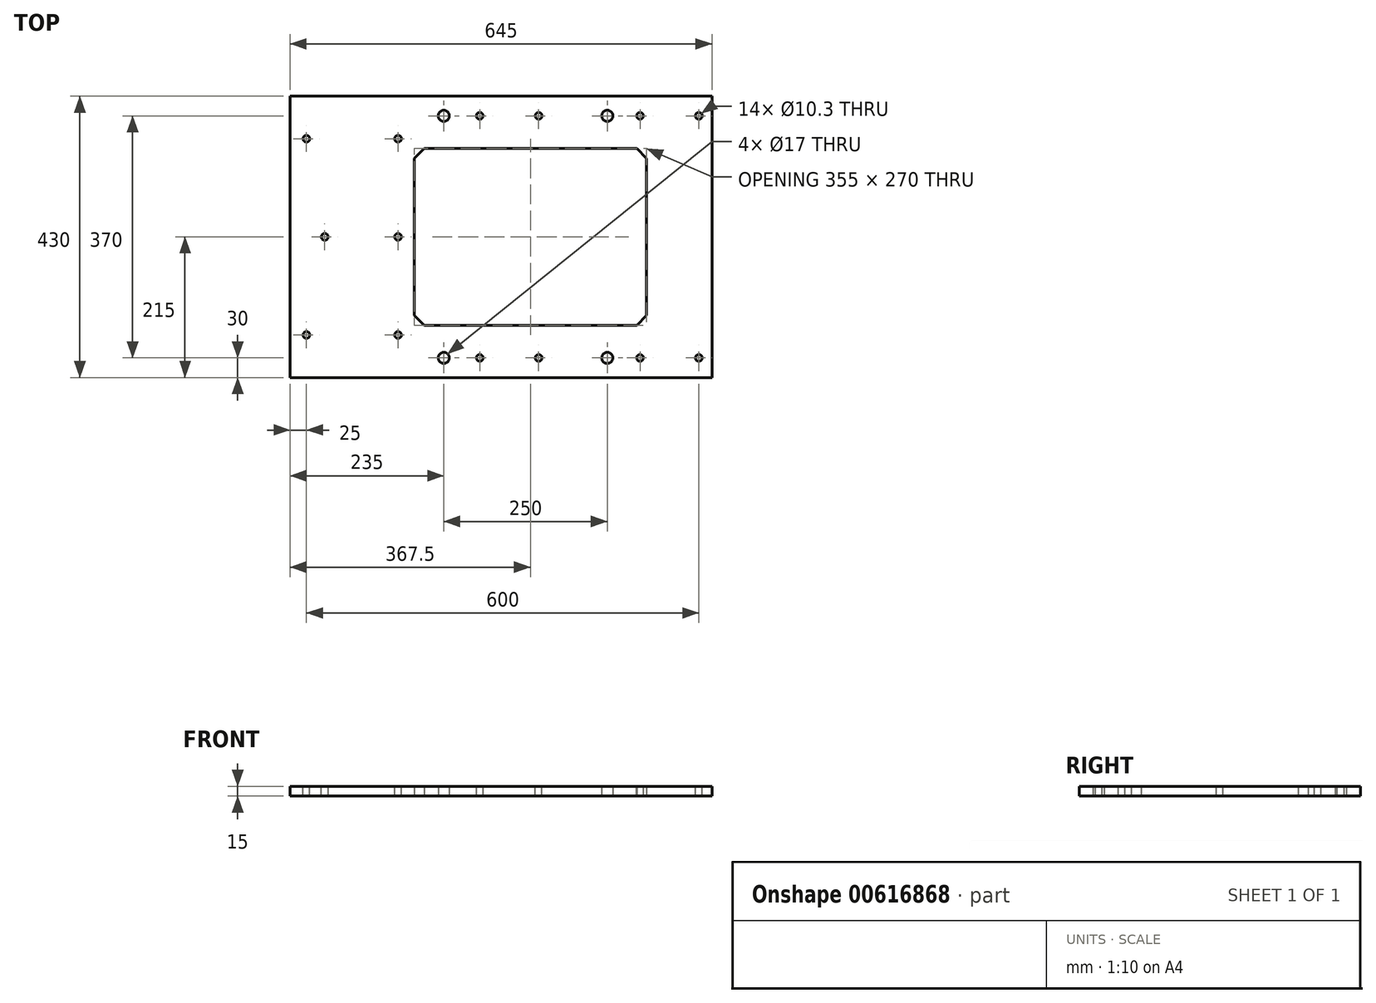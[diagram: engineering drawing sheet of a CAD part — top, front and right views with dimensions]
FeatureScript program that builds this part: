
annotation { "Feature Type Name" : "Feature", "Feature Type Description" : "" }
export const myFeature = defineFeature(function(context is Context, id is Id, definition is map)
    precondition{}
    {
        {
            var Q0;
            Q0=qCreatedBy(makeId("Top.planeOp"),FACE);
            var sketch = newSketch(context, id + "F0", { "sketchPlane" : qUnion([Q0])});
            skLineSegment(sketch, "E0.bottom", {"start": v(322.5, 215) * mm, "end": v(-322.5, 215) * mm});
            skLineSegment(sketch, "E0.top", {"start": v(322.5, -215) * mm, "end": v(-322.5, -215) * mm});
            skLineSegment(sketch, "E0.left", {"start": v(322.5, 215) * mm, "end": v(322.5, -215) * mm});
            skLineSegment(sketch, "E0.right", {"start": v(-322.5, 215) * mm, "end": v(-322.5, -215) * mm});
            skPoint(sketch, "E0.middle", {"position": v(0, 0) * mm});
            skLineSegment(sketch, "E1.bottom", {"start": v(-117.5, 135) * mm, "end": v(207.5, 135) * mm});
            skLineSegment(sketch, "E1.top", {"start": v(-117.5, -135) * mm, "end": v(207.5, -135) * mm});
            skLineSegment(sketch, "E1.left", {"start": v(-132.5, 120) * mm, "end": v(-132.5, -120) * mm});
            skLineSegment(sketch, "E1.right", {"start": v(222.5, 120) * mm, "end": v(222.5, -120) * mm});
            skLineSegment(sketch, "E2", {"start": v(-132.5, 120) * mm, "end": v(-117.5, 135) * mm});
            skLineSegment(sketch, "E3", {"start": v(207.5, 135) * mm, "end": v(222.5, 120) * mm});
            skLineSegment(sketch, "E4", {"start": v(-132.5, -120) * mm, "end": v(-117.5, -135) * mm});
            skLineSegment(sketch, "E5", {"start": v(207.5, -135) * mm, "end": v(222.5, -120) * mm});
            skSolve(sketch);
        }
        {
            var Q0;
            Q0=qSketchRegion(id+"F0",true);
            extrude(context, id + "F1", {"entities" : qUnion([Q0]), "depth" : 15 * mm, "offsetDistance" : 25 * mm});
        }
        {
            var Q0;
            Q0=qCreatedBy(makeId("Top.planeOp"),FACE);
            var sketch = newSketch(context, id + "F2", { "sketchPlane" : qUnion([Q0])});
            skLineSegment(sketch, "E6.0", {"start": v(322.5, 215) * mm, "end": v(-322.5, 215) * mm, "construction": true});
            skLineSegment(sketch, "E7.0", {"start": v(322.5, 215) * mm, "end": v(322.5, -215) * mm, "construction": true});
            skLineSegment(sketch, "E8.0", {"start": v(322.5, -215) * mm, "end": v(-322.5, -215) * mm, "construction": true});
            skLineSegment(sketch, "E9.0", {"start": v(-322.5, 215) * mm, "end": v(-322.5, -215) * mm, "construction": true});
            skLineSegment(sketch, "E10", {"start": v(-297.5, 215) * mm, "end": v(-297.5, -215) * mm, "construction": true});
            skLineSegment(sketch, "E11", {"start": v(-157.5, 215) * mm, "end": v(-157.5, -215) * mm, "construction": true});
            skLineSegment(sketch, "E12", {"start": v(-32.5, 215) * mm, "end": v(-32.5, -215) * mm, "construction": true});
            skLineSegment(sketch, "E13", {"start": v(57.5, 215) * mm, "end": v(57.5, -215) * mm, "construction": true});
            skLineSegment(sketch, "E14", {"start": v(212.5, 215) * mm, "end": v(212.5, -215) * mm, "construction": true});
            skLineSegment(sketch, "E15", {"start": v(302.5, 215) * mm, "end": v(302.5, -215) * mm, "construction": true});
            skLineSegment(sketch, "E16", {"start": v(322.5, 185) * mm, "end": v(-322.5, 185) * mm, "construction": true});
            skLineSegment(sketch, "E17", {"start": v(322.5, -185) * mm, "end": v(-322.5, -185) * mm, "construction": true});
            skPoint(sketch, "E18", {"position": v(302.5, 185) * mm});
            skPoint(sketch, "E19", {"position": v(212.5, 185) * mm});
            skPoint(sketch, "E20", {"position": v(57.5, 185) * mm});
            skPoint(sketch, "E21", {"position": v(-32.5, 185) * mm});
            skPoint(sketch, "E22", {"position": v(-32.5, -185) * mm});
            skPoint(sketch, "E23", {"position": v(57.5, -185) * mm});
            skPoint(sketch, "E24", {"position": v(302.5, -185) * mm});
            skPoint(sketch, "E25", {"position": v(212.5, -185) * mm});
            skLineSegment(sketch, "E26", {"start": v(-322.5, 150) * mm, "end": v(-157.5, 150) * mm, "construction": true});
            skLineSegment(sketch, "E27", {"start": v(-322.5, 0) * mm, "end": v(-157.5, 0) * mm, "construction": true});
            skLineSegment(sketch, "E28", {"start": v(-322.5, -150) * mm, "end": v(-157.5, -150) * mm, "construction": true});
            skPoint(sketch, "E29", {"position": v(-157.5, 150) * mm});
            skPoint(sketch, "E30", {"position": v(-297.5, 150) * mm});
            skPoint(sketch, "E31", {"position": v(-157.5, 0) * mm});
            skPoint(sketch, "E32", {"position": v(-297.5, 0) * mm});
            skPoint(sketch, "E33", {"position": v(-297.5, -150) * mm});
            skPoint(sketch, "E34", {"position": v(-157.5, -150) * mm});
            skPoint(sketch, "E35", {"position": v(-269.5, 0) * mm});
            skSolve(sketch);
        }
        {
            var Q0;
            Q0=sQuery(id+"F2.wireOp",VERTEX,"E30");
            var Q1;
            Q1=sQuery(id+"F2.wireOp",VERTEX,"E33");
            var Q2;
            Q2=sQuery(id+"F2.wireOp",VERTEX,"E29");
            var Q3;
            Q3=sQuery(id+"F2.wireOp",VERTEX,"E31");
            var Q4;
            Q4=sQuery(id+"F2.wireOp",VERTEX,"E34");
            var Q5;
            Q5=sQuery(id+"F2.wireOp",VERTEX,"E22");
            var Q6;
            Q6=sQuery(id+"F2.wireOp",VERTEX,"E23");
            var Q7;
            Q7=sQuery(id+"F2.wireOp",VERTEX,"E25");
            var Q8;
            Q8=sQuery(id+"F2.wireOp",VERTEX,"E24");
            var Q9;
            Q9=sQuery(id+"F2.wireOp",VERTEX,"E18");
            var Q10;
            Q10=sQuery(id+"F2.wireOp",VERTEX,"E19");
            var Q11;
            Q11=sQuery(id+"F2.wireOp",VERTEX,"E20");
            var Q12;
            Q12=sQuery(id+"F2.wireOp",VERTEX,"E21");
            var Q13;
            Q13=sQuery(id+"F2.wireOp",VERTEX,"E35");
            var Q14;
            Q14=makeQuery(id+"F1.opExtrude","SWEPT_BODY",BODY,{"disambiguationData":[OSD([sQuery(id+"F0.wireOp",EDGE,"E0.bottom"),sQuery(id+"F0.wireOp",EDGE,"E0.top"),sQuery(id+"F0.wireOp",EDGE,"E0.left"),sQuery(id+"F0.wireOp",EDGE,"E0.right"),sQuery(id+"F0.wireOp",EDGE,"E1.bottom"),sQuery(id+"F0.wireOp",EDGE,"E1.top"),sQuery(id+"F0.wireOp",EDGE,"E1.left"),sQuery(id+"F0.wireOp",EDGE,"E1.right"),sQuery(id+"F0.wireOp",EDGE,"E2"),sQuery(id+"F0.wireOp",EDGE,"E3"),sQuery(id+"F0.wireOp",EDGE,"E4"),sQuery(id+"F0.wireOp",EDGE,"E5")])]});
            hole(context, id + "F3", {"style" : HoleStyle.SIMPLE, "endStyle" : HoleEndStyle.THROUGH, "oppositeDirection" : true, "standardTappedOrClearance" : lookupTablePath({ "standard" : "ISO", "engagement" : "75%", "pitch" : "1.75 mm", "size" : "M12", "type" : "Tapped" }), "standardBlindInLast" : lookupTablePath({ "standard" : "ISO", "engagement" : "75%", "pitch" : "1.75 mm", "size" : "M12", "type" : "Tapped" }), "holeDiameter" : 10.3 * mm, "majorDiameter" : 12 * mm, "showTappedDepth" : true, "isTappedThrough" : true, "tappedDepth" : 12 * mm, "tapClearance" : 3, "locations" : qUnion([Q0, Q1, Q2, Q3, Q4, Q5, Q6, Q7, Q8, Q9, Q10, Q11, Q12, Q13]), "scope" : qUnion([Q14]), "startStyle" : HoleStartStyle.PART});
        }
        {
            var Q0;
            Q0=qCreatedBy(makeId("Top.planeOp"),FACE);
            var sketch = newSketch(context, id + "F4", { "sketchPlane" : qUnion([Q0])});
            skLineSegment(sketch, "E36.0", {"start": v(322.5, 215) * mm, "end": v(-322.5, 215) * mm, "construction": true});
            skLineSegment(sketch, "E37.0", {"start": v(322.5, 215) * mm, "end": v(322.5, -215) * mm, "construction": true});
            skLineSegment(sketch, "E38.0", {"start": v(322.5, -215) * mm, "end": v(-322.5, -215) * mm, "construction": true});
            skLineSegment(sketch, "E39.0", {"start": v(-322.5, 215) * mm, "end": v(-322.5, -215) * mm, "construction": true});
            skLineSegment(sketch, "E40", {"start": v(322.5, -185) * mm, "end": v(-322.5, -185) * mm, "construction": true});
            skLineSegment(sketch, "E41", {"start": v(322.5, 185) * mm, "end": v(-322.5, 185) * mm, "construction": true});
            skLineSegment(sketch, "E42", {"start": v(162.5, 215) * mm, "end": v(162.5, -215) * mm, "construction": true});
            skLineSegment(sketch, "E43", {"start": v(-87.5, 215) * mm, "end": v(-87.5, -215) * mm, "construction": true});
            skCircle(sketch, "E44", {"center": v(-87.5, 185) * mm, "radius": 8.5 * mm});
            skCircle(sketch, "E45", {"center": v(162.5, 185) * mm, "radius": 8.5 * mm});
            skCircle(sketch, "E46", {"center": v(162.5, -185) * mm, "radius": 8.5 * mm});
            skCircle(sketch, "E47", {"center": v(-87.5, -185) * mm, "radius": 8.5 * mm});
            skSolve(sketch);
        }
        {
            var Q0;
            Q0=qSketchRegion(id+"F4",true);
            extrude(context, id + "F5", {"entities" : qUnion([Q0]), "operationType" : NewBodyOperationType.REMOVE, "endBound" : BoundingType.UP_TO_NEXT, "depth" : 25 * mm, "offsetDistance" : 25 * mm});
        }
    });
